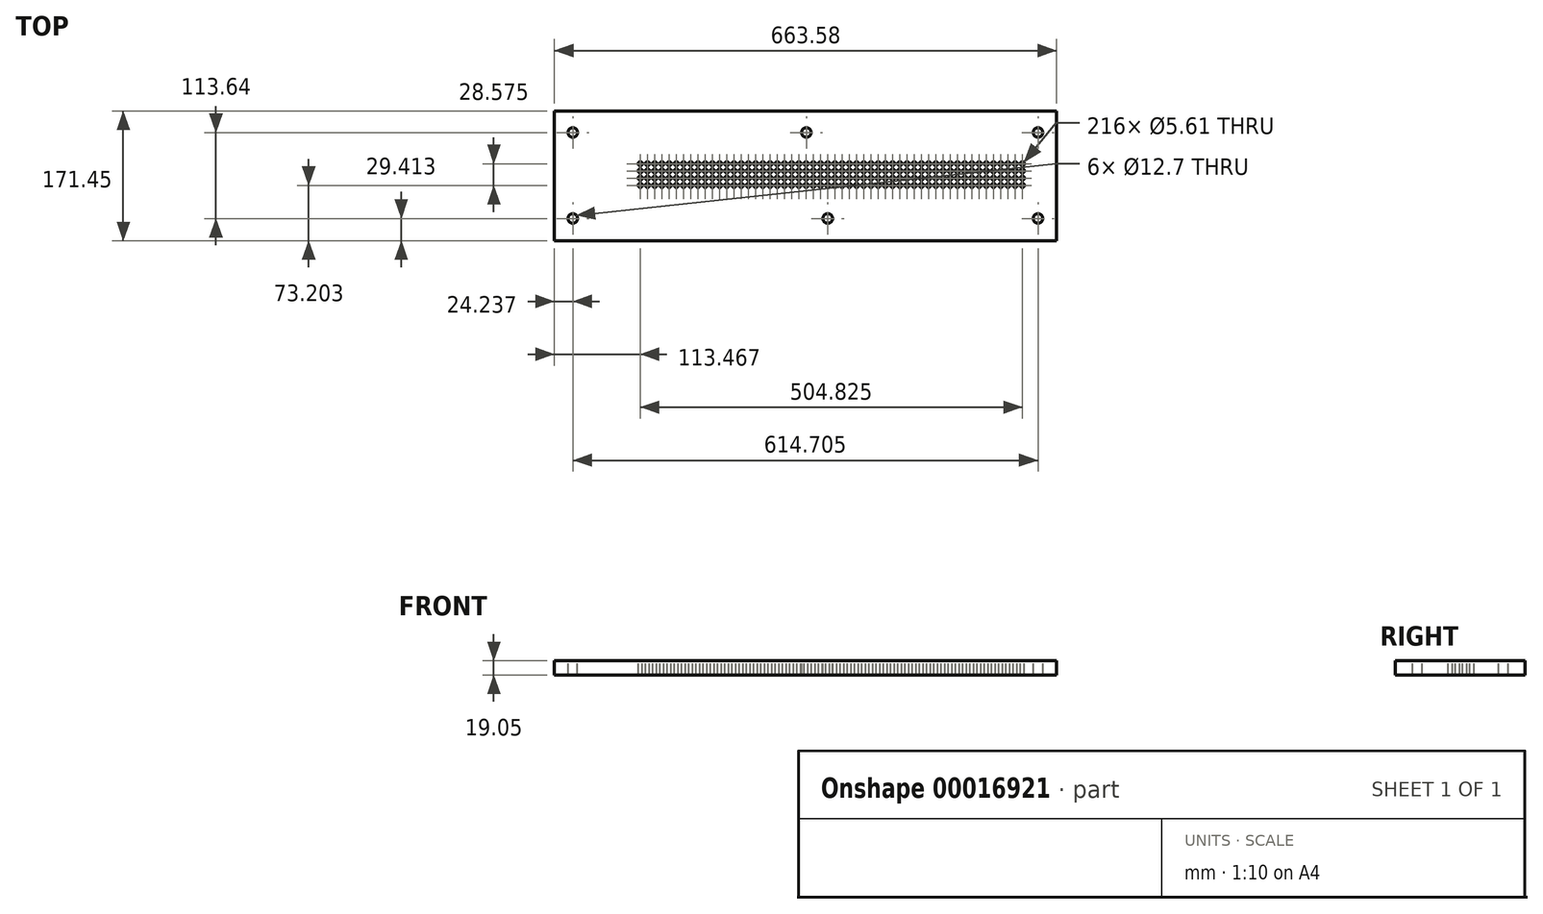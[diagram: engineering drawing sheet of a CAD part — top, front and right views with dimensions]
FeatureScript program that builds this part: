
annotation { "Feature Type Name" : "Feature", "Feature Type Description" : "" }
export const myFeature = defineFeature(function(context is Context, id is Id, definition is map)
    precondition{}
    {
        {
            var Q0;
            Q0=qCreatedBy(makeId("Top.planeOp"),FACE);
            var sketch = newSketch(context, id + "F0", { "sketchPlane" : qUnion([Q0])});
            skLineSegment(sketch, "E0.bottom", {"start": v(0, 0) * mm, "end": v(-663.58, 0) * mm});
            skLineSegment(sketch, "E0.top", {"start": v(0, -171.45) * mm, "end": v(-663.58, -171.45) * mm});
            skLineSegment(sketch, "E0.left", {"start": v(0, 0) * mm, "end": v(0, -171.45) * mm});
            skLineSegment(sketch, "E0.right", {"start": v(-663.58, 0) * mm, "end": v(-663.58, -171.45) * mm});
            skSolve(sketch);
        }
        {
            var Q0;
            Q0 = qSketchRegion(id + "F0", true);
            extrude(context, id + "F1", {"entities" : qUnion([Q0]), "oppositeDirection" : true, "depth" : 19.05 * mm});
        }
        {
            var Q0;
            Q0=makeQuery(id+"F1.opExtrude","CAP_FACE",FACE,{"disambiguationData":[OSD([sQuery(id+"F0.wireOp",EDGE,"E0.bottom"),sQuery(id+"F0.wireOp",EDGE,"E0.top"),sQuery(id+"F0.wireOp",EDGE,"E0.left"),sQuery(id+"F0.wireOp",EDGE,"E0.right")])],"isStart":true});
            var sketch = newSketch(context, id + "F2", { "sketchPlane" : qUnion([Q0])});
            skCircle(sketch, "E1", {"center": v(-24.64, -28.4) * mm, "radius": 6.35 * mm});
            skCircle(sketch, "E2", {"center": v(-330.7, -28.4) * mm, "radius": 6.35 * mm});
            skCircle(sketch, "E3", {"center": v(-639.34, -28.4) * mm, "radius": 6.35 * mm});
            skCircle(sketch, "E4", {"center": v(-639.34, -142.04) * mm, "radius": 6.35 * mm});
            skCircle(sketch, "E5", {"center": v(-302.49, -142.04) * mm, "radius": 6.35 * mm});
            skCircle(sketch, "E6", {"center": v(-24.64, -142.04) * mm, "radius": 6.35 * mm});
            skSolve(sketch);
        }
        {
            var Q0;
            Q0 = qSketchRegion(id + "F2", true);
            extrude(context, id + "F3", {"entities" : qUnion([Q0]), "operationType" : NewBodyOperationType.REMOVE, "endBound" : BoundingType.THROUGH_ALL, "oppositeDirection" : true, "depth" : 25.4 * mm});
        }
        {
            var Q0;
            Q0=makeQuery(id+"F1.opExtrude","CAP_FACE",FACE,{"disambiguationData":[OSD([sQuery(id+"F0.wireOp",EDGE,"E0.bottom"),sQuery(id+"F0.wireOp",EDGE,"E0.top"),sQuery(id+"F0.wireOp",EDGE,"E0.left"),sQuery(id+"F0.wireOp",EDGE,"E0.right")])],"isStart":true});
            var sketch = newSketch(context, id + "F4", { "sketchPlane" : qUnion([Q0])});
            skCircle(sketch, "E7", {"center": v(-45.29, -69.67) * mm, "radius": 2.8 * mm});
            skCircle(sketch, "E8.0.1.0", {"center": v(-45.29, -79.2) * mm, "radius": 2.8 * mm});
            skCircle(sketch, "E8.0.2.0", {"center": v(-45.29, -88.72) * mm, "radius": 2.8 * mm});
            skCircle(sketch, "E8.0.3.0", {"center": v(-45.29, -98.25) * mm, "radius": 2.8 * mm});
            skCircle(sketch, "E8.1.0.0", {"center": v(-54.81, -69.67) * mm, "radius": 2.8 * mm});
            skCircle(sketch, "E8.1.1.0", {"center": v(-54.81, -79.2) * mm, "radius": 2.8 * mm});
            skCircle(sketch, "E8.1.2.0", {"center": v(-54.81, -88.72) * mm, "radius": 2.8 * mm});
            skCircle(sketch, "E8.1.3.0", {"center": v(-54.81, -98.25) * mm, "radius": 2.8 * mm});
            skCircle(sketch, "E8.2.0.0", {"center": v(-64.34, -69.67) * mm, "radius": 2.8 * mm});
            skCircle(sketch, "E8.2.1.0", {"center": v(-64.34, -79.2) * mm, "radius": 2.8 * mm});
            skCircle(sketch, "E8.2.2.0", {"center": v(-64.34, -88.72) * mm, "radius": 2.8 * mm});
            skCircle(sketch, "E8.2.3.0", {"center": v(-64.34, -98.25) * mm, "radius": 2.8 * mm});
            skCircle(sketch, "E8.3.0.0", {"center": v(-73.86, -69.67) * mm, "radius": 2.8 * mm});
            skCircle(sketch, "E8.3.1.0", {"center": v(-73.86, -79.2) * mm, "radius": 2.8 * mm});
            skCircle(sketch, "E8.3.2.0", {"center": v(-73.86, -88.72) * mm, "radius": 2.8 * mm});
            skCircle(sketch, "E8.3.3.0", {"center": v(-73.86, -98.25) * mm, "radius": 2.8 * mm});
            skCircle(sketch, "E8.4.0.0", {"center": v(-83.39, -69.67) * mm, "radius": 2.8 * mm});
            skCircle(sketch, "E8.4.1.0", {"center": v(-83.39, -79.2) * mm, "radius": 2.8 * mm});
            skCircle(sketch, "E8.4.2.0", {"center": v(-83.39, -88.72) * mm, "radius": 2.8 * mm});
            skCircle(sketch, "E8.4.3.0", {"center": v(-83.39, -98.25) * mm, "radius": 2.8 * mm});
            skCircle(sketch, "E8.5.0.0", {"center": v(-92.91, -69.67) * mm, "radius": 2.8 * mm});
            skCircle(sketch, "E8.5.1.0", {"center": v(-92.91, -79.2) * mm, "radius": 2.8 * mm});
            skCircle(sketch, "E8.5.2.0", {"center": v(-92.91, -88.72) * mm, "radius": 2.8 * mm});
            skCircle(sketch, "E8.5.3.0", {"center": v(-92.91, -98.25) * mm, "radius": 2.8 * mm});
            skCircle(sketch, "E8.6.0.0", {"center": v(-102.44, -69.67) * mm, "radius": 2.8 * mm});
            skCircle(sketch, "E8.6.1.0", {"center": v(-102.44, -79.2) * mm, "radius": 2.8 * mm});
            skCircle(sketch, "E8.6.2.0", {"center": v(-102.44, -88.72) * mm, "radius": 2.8 * mm});
            skCircle(sketch, "E8.6.3.0", {"center": v(-102.44, -98.25) * mm, "radius": 2.8 * mm});
            skCircle(sketch, "E8.7.0.0", {"center": v(-111.96, -69.67) * mm, "radius": 2.8 * mm});
            skCircle(sketch, "E8.7.1.0", {"center": v(-111.96, -79.2) * mm, "radius": 2.8 * mm});
            skCircle(sketch, "E8.7.2.0", {"center": v(-111.96, -88.72) * mm, "radius": 2.8 * mm});
            skCircle(sketch, "E8.7.3.0", {"center": v(-111.96, -98.25) * mm, "radius": 2.8 * mm});
            skCircle(sketch, "E8.8.0.0", {"center": v(-121.49, -69.67) * mm, "radius": 2.8 * mm});
            skCircle(sketch, "E8.8.1.0", {"center": v(-121.49, -79.2) * mm, "radius": 2.8 * mm});
            skCircle(sketch, "E8.8.2.0", {"center": v(-121.49, -88.72) * mm, "radius": 2.8 * mm});
            skCircle(sketch, "E8.8.3.0", {"center": v(-121.49, -98.25) * mm, "radius": 2.8 * mm});
            skCircle(sketch, "E8.9.0.0", {"center": v(-131.01, -69.67) * mm, "radius": 2.8 * mm});
            skCircle(sketch, "E8.9.1.0", {"center": v(-131.01, -79.2) * mm, "radius": 2.8 * mm});
            skCircle(sketch, "E8.9.2.0", {"center": v(-131.01, -88.72) * mm, "radius": 2.8 * mm});
            skCircle(sketch, "E8.9.3.0", {"center": v(-131.01, -98.25) * mm, "radius": 2.8 * mm});
            skCircle(sketch, "E8.10.0.0", {"center": v(-140.54, -69.67) * mm, "radius": 2.8 * mm});
            skCircle(sketch, "E8.10.1.0", {"center": v(-140.54, -79.2) * mm, "radius": 2.8 * mm});
            skCircle(sketch, "E8.10.2.0", {"center": v(-140.54, -88.72) * mm, "radius": 2.8 * mm});
            skCircle(sketch, "E8.10.3.0", {"center": v(-140.54, -98.25) * mm, "radius": 2.8 * mm});
            skCircle(sketch, "E8.11.0.0", {"center": v(-150.06, -69.67) * mm, "radius": 2.8 * mm});
            skCircle(sketch, "E8.11.1.0", {"center": v(-150.06, -79.2) * mm, "radius": 2.8 * mm});
            skCircle(sketch, "E8.11.2.0", {"center": v(-150.06, -88.72) * mm, "radius": 2.8 * mm});
            skCircle(sketch, "E8.11.3.0", {"center": v(-150.06, -98.25) * mm, "radius": 2.8 * mm});
            skCircle(sketch, "E8.12.0.0", {"center": v(-159.59, -69.67) * mm, "radius": 2.8 * mm});
            skCircle(sketch, "E8.12.1.0", {"center": v(-159.59, -79.2) * mm, "radius": 2.8 * mm});
            skCircle(sketch, "E8.12.2.0", {"center": v(-159.59, -88.72) * mm, "radius": 2.8 * mm});
            skCircle(sketch, "E8.12.3.0", {"center": v(-159.59, -98.25) * mm, "radius": 2.8 * mm});
            skCircle(sketch, "E8.13.0.0", {"center": v(-169.11, -69.67) * mm, "radius": 2.8 * mm});
            skCircle(sketch, "E8.13.1.0", {"center": v(-169.11, -79.2) * mm, "radius": 2.8 * mm});
            skCircle(sketch, "E8.13.2.0", {"center": v(-169.11, -88.72) * mm, "radius": 2.8 * mm});
            skCircle(sketch, "E8.13.3.0", {"center": v(-169.11, -98.25) * mm, "radius": 2.8 * mm});
            skCircle(sketch, "E8.14.0.0", {"center": v(-178.64, -69.67) * mm, "radius": 2.8 * mm});
            skCircle(sketch, "E8.14.1.0", {"center": v(-178.64, -79.2) * mm, "radius": 2.8 * mm});
            skCircle(sketch, "E8.14.2.0", {"center": v(-178.64, -88.72) * mm, "radius": 2.8 * mm});
            skCircle(sketch, "E8.14.3.0", {"center": v(-178.64, -98.25) * mm, "radius": 2.8 * mm});
            skCircle(sketch, "E8.15.0.0", {"center": v(-188.16, -69.67) * mm, "radius": 2.8 * mm});
            skCircle(sketch, "E8.15.1.0", {"center": v(-188.16, -79.2) * mm, "radius": 2.8 * mm});
            skCircle(sketch, "E8.15.2.0", {"center": v(-188.16, -88.72) * mm, "radius": 2.8 * mm});
            skCircle(sketch, "E8.15.3.0", {"center": v(-188.16, -98.25) * mm, "radius": 2.8 * mm});
            skCircle(sketch, "E8.16.0.0", {"center": v(-197.69, -69.67) * mm, "radius": 2.8 * mm});
            skCircle(sketch, "E8.16.1.0", {"center": v(-197.69, -79.2) * mm, "radius": 2.8 * mm});
            skCircle(sketch, "E8.16.2.0", {"center": v(-197.69, -88.72) * mm, "radius": 2.8 * mm});
            skCircle(sketch, "E8.16.3.0", {"center": v(-197.69, -98.25) * mm, "radius": 2.8 * mm});
            skCircle(sketch, "E8.17.0.0", {"center": v(-207.21, -69.67) * mm, "radius": 2.8 * mm});
            skCircle(sketch, "E8.17.1.0", {"center": v(-207.21, -79.2) * mm, "radius": 2.8 * mm});
            skCircle(sketch, "E8.17.2.0", {"center": v(-207.21, -88.72) * mm, "radius": 2.8 * mm});
            skCircle(sketch, "E8.17.3.0", {"center": v(-207.21, -98.25) * mm, "radius": 2.8 * mm});
            skCircle(sketch, "E8.18.0.0", {"center": v(-216.74, -69.67) * mm, "radius": 2.8 * mm});
            skCircle(sketch, "E8.18.1.0", {"center": v(-216.74, -79.2) * mm, "radius": 2.8 * mm});
            skCircle(sketch, "E8.18.2.0", {"center": v(-216.74, -88.72) * mm, "radius": 2.8 * mm});
            skCircle(sketch, "E8.18.3.0", {"center": v(-216.74, -98.25) * mm, "radius": 2.8 * mm});
            skCircle(sketch, "E8.19.0.0", {"center": v(-226.26, -69.67) * mm, "radius": 2.8 * mm});
            skCircle(sketch, "E8.19.1.0", {"center": v(-226.26, -79.2) * mm, "radius": 2.8 * mm});
            skCircle(sketch, "E8.19.2.0", {"center": v(-226.26, -88.72) * mm, "radius": 2.8 * mm});
            skCircle(sketch, "E8.19.3.0", {"center": v(-226.26, -98.25) * mm, "radius": 2.8 * mm});
            skCircle(sketch, "E8.20.0.0", {"center": v(-235.79, -69.67) * mm, "radius": 2.8 * mm});
            skCircle(sketch, "E8.20.1.0", {"center": v(-235.79, -79.2) * mm, "radius": 2.8 * mm});
            skCircle(sketch, "E8.20.2.0", {"center": v(-235.79, -88.72) * mm, "radius": 2.8 * mm});
            skCircle(sketch, "E8.20.3.0", {"center": v(-235.79, -98.25) * mm, "radius": 2.8 * mm});
            skCircle(sketch, "E8.21.0.0", {"center": v(-245.31, -69.67) * mm, "radius": 2.8 * mm});
            skCircle(sketch, "E8.21.1.0", {"center": v(-245.31, -79.2) * mm, "radius": 2.8 * mm});
            skCircle(sketch, "E8.21.2.0", {"center": v(-245.31, -88.72) * mm, "radius": 2.8 * mm});
            skCircle(sketch, "E8.21.3.0", {"center": v(-245.31, -98.25) * mm, "radius": 2.8 * mm});
            skCircle(sketch, "E8.22.0.0", {"center": v(-254.84, -69.67) * mm, "radius": 2.8 * mm});
            skCircle(sketch, "E8.22.1.0", {"center": v(-254.84, -79.2) * mm, "radius": 2.8 * mm});
            skCircle(sketch, "E8.22.2.0", {"center": v(-254.84, -88.72) * mm, "radius": 2.8 * mm});
            skCircle(sketch, "E8.22.3.0", {"center": v(-254.84, -98.25) * mm, "radius": 2.8 * mm});
            skCircle(sketch, "E8.23.0.0", {"center": v(-264.36, -69.67) * mm, "radius": 2.8 * mm});
            skCircle(sketch, "E8.23.1.0", {"center": v(-264.36, -79.2) * mm, "radius": 2.8 * mm});
            skCircle(sketch, "E8.23.2.0", {"center": v(-264.36, -88.72) * mm, "radius": 2.8 * mm});
            skCircle(sketch, "E8.23.3.0", {"center": v(-264.36, -98.25) * mm, "radius": 2.8 * mm});
            skCircle(sketch, "E8.24.0.0", {"center": v(-273.89, -69.67) * mm, "radius": 2.8 * mm});
            skCircle(sketch, "E8.24.1.0", {"center": v(-273.89, -79.2) * mm, "radius": 2.8 * mm});
            skCircle(sketch, "E8.24.2.0", {"center": v(-273.89, -88.72) * mm, "radius": 2.8 * mm});
            skCircle(sketch, "E8.24.3.0", {"center": v(-273.89, -98.25) * mm, "radius": 2.8 * mm});
            skCircle(sketch, "E8.25.0.0", {"center": v(-283.41, -69.67) * mm, "radius": 2.8 * mm});
            skCircle(sketch, "E8.25.1.0", {"center": v(-283.41, -79.2) * mm, "radius": 2.8 * mm});
            skCircle(sketch, "E8.25.2.0", {"center": v(-283.41, -88.72) * mm, "radius": 2.8 * mm});
            skCircle(sketch, "E8.25.3.0", {"center": v(-283.41, -98.25) * mm, "radius": 2.8 * mm});
            skCircle(sketch, "E8.26.0.0", {"center": v(-292.94, -69.67) * mm, "radius": 2.8 * mm});
            skCircle(sketch, "E8.26.1.0", {"center": v(-292.94, -79.2) * mm, "radius": 2.8 * mm});
            skCircle(sketch, "E8.26.2.0", {"center": v(-292.94, -88.72) * mm, "radius": 2.8 * mm});
            skCircle(sketch, "E8.26.3.0", {"center": v(-292.94, -98.25) * mm, "radius": 2.8 * mm});
            skCircle(sketch, "E8.27.0.0", {"center": v(-302.46, -69.67) * mm, "radius": 2.8 * mm});
            skCircle(sketch, "E8.27.1.0", {"center": v(-302.46, -79.2) * mm, "radius": 2.8 * mm});
            skCircle(sketch, "E8.27.2.0", {"center": v(-302.46, -88.72) * mm, "radius": 2.8 * mm});
            skCircle(sketch, "E8.27.3.0", {"center": v(-302.46, -98.25) * mm, "radius": 2.8 * mm});
            skCircle(sketch, "E8.28.0.0", {"center": v(-311.99, -69.67) * mm, "radius": 2.8 * mm});
            skCircle(sketch, "E8.28.1.0", {"center": v(-311.99, -79.2) * mm, "radius": 2.8 * mm});
            skCircle(sketch, "E8.28.2.0", {"center": v(-311.99, -88.72) * mm, "radius": 2.8 * mm});
            skCircle(sketch, "E8.28.3.0", {"center": v(-311.99, -98.25) * mm, "radius": 2.8 * mm});
            skCircle(sketch, "E8.29.0.0", {"center": v(-321.51, -69.67) * mm, "radius": 2.8 * mm});
            skCircle(sketch, "E8.29.1.0", {"center": v(-321.51, -79.2) * mm, "radius": 2.8 * mm});
            skCircle(sketch, "E8.29.2.0", {"center": v(-321.51, -88.72) * mm, "radius": 2.8 * mm});
            skCircle(sketch, "E8.29.3.0", {"center": v(-321.51, -98.25) * mm, "radius": 2.8 * mm});
            skCircle(sketch, "E8.30.0.0", {"center": v(-331.04, -69.67) * mm, "radius": 2.8 * mm});
            skCircle(sketch, "E8.30.1.0", {"center": v(-331.04, -79.2) * mm, "radius": 2.8 * mm});
            skCircle(sketch, "E8.30.2.0", {"center": v(-331.04, -88.72) * mm, "radius": 2.8 * mm});
            skCircle(sketch, "E8.30.3.0", {"center": v(-331.04, -98.25) * mm, "radius": 2.8 * mm});
            skCircle(sketch, "E8.31.0.0", {"center": v(-340.56, -69.67) * mm, "radius": 2.8 * mm});
            skCircle(sketch, "E8.31.1.0", {"center": v(-340.56, -79.2) * mm, "radius": 2.8 * mm});
            skCircle(sketch, "E8.31.2.0", {"center": v(-340.56, -88.72) * mm, "radius": 2.8 * mm});
            skCircle(sketch, "E8.31.3.0", {"center": v(-340.56, -98.25) * mm, "radius": 2.8 * mm});
            skCircle(sketch, "E8.32.0.0", {"center": v(-350.09, -69.67) * mm, "radius": 2.8 * mm});
            skCircle(sketch, "E8.32.1.0", {"center": v(-350.09, -79.2) * mm, "radius": 2.8 * mm});
            skCircle(sketch, "E8.32.2.0", {"center": v(-350.09, -88.72) * mm, "radius": 2.8 * mm});
            skCircle(sketch, "E8.32.3.0", {"center": v(-350.09, -98.25) * mm, "radius": 2.8 * mm});
            skCircle(sketch, "E8.33.0.0", {"center": v(-359.61, -69.67) * mm, "radius": 2.8 * mm});
            skCircle(sketch, "E8.33.1.0", {"center": v(-359.61, -79.2) * mm, "radius": 2.8 * mm});
            skCircle(sketch, "E8.33.2.0", {"center": v(-359.61, -88.72) * mm, "radius": 2.8 * mm});
            skCircle(sketch, "E8.33.3.0", {"center": v(-359.61, -98.25) * mm, "radius": 2.8 * mm});
            skCircle(sketch, "E8.34.0.0", {"center": v(-369.14, -69.67) * mm, "radius": 2.8 * mm});
            skCircle(sketch, "E8.34.1.0", {"center": v(-369.14, -79.2) * mm, "radius": 2.8 * mm});
            skCircle(sketch, "E8.34.2.0", {"center": v(-369.14, -88.72) * mm, "radius": 2.8 * mm});
            skCircle(sketch, "E8.34.3.0", {"center": v(-369.14, -98.25) * mm, "radius": 2.8 * mm});
            skCircle(sketch, "E8.35.0.0", {"center": v(-378.66, -69.67) * mm, "radius": 2.8 * mm});
            skCircle(sketch, "E8.35.1.0", {"center": v(-378.66, -79.2) * mm, "radius": 2.8 * mm});
            skCircle(sketch, "E8.35.2.0", {"center": v(-378.66, -88.72) * mm, "radius": 2.8 * mm});
            skCircle(sketch, "E8.35.3.0", {"center": v(-378.66, -98.25) * mm, "radius": 2.8 * mm});
            skCircle(sketch, "E8.36.0.0", {"center": v(-388.19, -69.67) * mm, "radius": 2.8 * mm});
            skCircle(sketch, "E8.36.1.0", {"center": v(-388.19, -79.2) * mm, "radius": 2.8 * mm});
            skCircle(sketch, "E8.36.2.0", {"center": v(-388.19, -88.72) * mm, "radius": 2.8 * mm});
            skCircle(sketch, "E8.36.3.0", {"center": v(-388.19, -98.25) * mm, "radius": 2.8 * mm});
            skCircle(sketch, "E8.37.0.0", {"center": v(-397.71, -69.67) * mm, "radius": 2.8 * mm});
            skCircle(sketch, "E8.37.1.0", {"center": v(-397.71, -79.2) * mm, "radius": 2.8 * mm});
            skCircle(sketch, "E8.37.2.0", {"center": v(-397.71, -88.72) * mm, "radius": 2.8 * mm});
            skCircle(sketch, "E8.37.3.0", {"center": v(-397.71, -98.25) * mm, "radius": 2.8 * mm});
            skCircle(sketch, "E8.38.0.0", {"center": v(-407.24, -69.67) * mm, "radius": 2.8 * mm});
            skCircle(sketch, "E8.38.1.0", {"center": v(-407.24, -79.2) * mm, "radius": 2.8 * mm});
            skCircle(sketch, "E8.38.2.0", {"center": v(-407.24, -88.72) * mm, "radius": 2.8 * mm});
            skCircle(sketch, "E8.38.3.0", {"center": v(-407.24, -98.25) * mm, "radius": 2.8 * mm});
            skCircle(sketch, "E8.39.0.0", {"center": v(-416.76, -69.67) * mm, "radius": 2.8 * mm});
            skCircle(sketch, "E8.39.1.0", {"center": v(-416.76, -79.2) * mm, "radius": 2.8 * mm});
            skCircle(sketch, "E8.39.2.0", {"center": v(-416.76, -88.72) * mm, "radius": 2.8 * mm});
            skCircle(sketch, "E8.39.3.0", {"center": v(-416.76, -98.25) * mm, "radius": 2.8 * mm});
            skCircle(sketch, "E8.40.0.0", {"center": v(-426.29, -69.67) * mm, "radius": 2.8 * mm});
            skCircle(sketch, "E8.40.1.0", {"center": v(-426.29, -79.2) * mm, "radius": 2.8 * mm});
            skCircle(sketch, "E8.40.2.0", {"center": v(-426.29, -88.72) * mm, "radius": 2.8 * mm});
            skCircle(sketch, "E8.40.3.0", {"center": v(-426.29, -98.25) * mm, "radius": 2.8 * mm});
            skCircle(sketch, "E8.41.0.0", {"center": v(-435.81, -69.67) * mm, "radius": 2.8 * mm});
            skCircle(sketch, "E8.41.1.0", {"center": v(-435.81, -79.2) * mm, "radius": 2.8 * mm});
            skCircle(sketch, "E8.41.2.0", {"center": v(-435.81, -88.72) * mm, "radius": 2.8 * mm});
            skCircle(sketch, "E8.41.3.0", {"center": v(-435.81, -98.25) * mm, "radius": 2.8 * mm});
            skCircle(sketch, "E8.42.0.0", {"center": v(-445.34, -69.67) * mm, "radius": 2.8 * mm});
            skCircle(sketch, "E8.42.1.0", {"center": v(-445.34, -79.2) * mm, "radius": 2.8 * mm});
            skCircle(sketch, "E8.42.2.0", {"center": v(-445.34, -88.72) * mm, "radius": 2.8 * mm});
            skCircle(sketch, "E8.42.3.0", {"center": v(-445.34, -98.25) * mm, "radius": 2.8 * mm});
            skCircle(sketch, "E8.43.0.0", {"center": v(-454.86, -69.67) * mm, "radius": 2.8 * mm});
            skCircle(sketch, "E8.43.1.0", {"center": v(-454.86, -79.2) * mm, "radius": 2.8 * mm});
            skCircle(sketch, "E8.43.2.0", {"center": v(-454.86, -88.72) * mm, "radius": 2.8 * mm});
            skCircle(sketch, "E8.43.3.0", {"center": v(-454.86, -98.25) * mm, "radius": 2.8 * mm});
            skCircle(sketch, "E8.44.0.0", {"center": v(-464.39, -69.67) * mm, "radius": 2.8 * mm});
            skCircle(sketch, "E8.44.1.0", {"center": v(-464.39, -79.2) * mm, "radius": 2.8 * mm});
            skCircle(sketch, "E8.44.2.0", {"center": v(-464.39, -88.72) * mm, "radius": 2.8 * mm});
            skCircle(sketch, "E8.44.3.0", {"center": v(-464.39, -98.25) * mm, "radius": 2.8 * mm});
            skCircle(sketch, "E8.45.0.0", {"center": v(-473.91, -69.67) * mm, "radius": 2.8 * mm});
            skCircle(sketch, "E8.45.1.0", {"center": v(-473.91, -79.2) * mm, "radius": 2.8 * mm});
            skCircle(sketch, "E8.45.2.0", {"center": v(-473.91, -88.72) * mm, "radius": 2.8 * mm});
            skCircle(sketch, "E8.45.3.0", {"center": v(-473.91, -98.25) * mm, "radius": 2.8 * mm});
            skCircle(sketch, "E8.46.0.0", {"center": v(-483.44, -69.67) * mm, "radius": 2.8 * mm});
            skCircle(sketch, "E8.46.1.0", {"center": v(-483.44, -79.2) * mm, "radius": 2.8 * mm});
            skCircle(sketch, "E8.46.2.0", {"center": v(-483.44, -88.72) * mm, "radius": 2.8 * mm});
            skCircle(sketch, "E8.46.3.0", {"center": v(-483.44, -98.25) * mm, "radius": 2.8 * mm});
            skCircle(sketch, "E8.47.0.0", {"center": v(-492.96, -69.67) * mm, "radius": 2.8 * mm});
            skCircle(sketch, "E8.47.1.0", {"center": v(-492.96, -79.2) * mm, "radius": 2.8 * mm});
            skCircle(sketch, "E8.47.2.0", {"center": v(-492.96, -88.72) * mm, "radius": 2.8 * mm});
            skCircle(sketch, "E8.47.3.0", {"center": v(-492.96, -98.25) * mm, "radius": 2.8 * mm});
            skCircle(sketch, "E8.48.0.0", {"center": v(-502.49, -69.67) * mm, "radius": 2.8 * mm});
            skCircle(sketch, "E8.48.1.0", {"center": v(-502.49, -79.2) * mm, "radius": 2.8 * mm});
            skCircle(sketch, "E8.48.2.0", {"center": v(-502.49, -88.72) * mm, "radius": 2.8 * mm});
            skCircle(sketch, "E8.48.3.0", {"center": v(-502.49, -98.25) * mm, "radius": 2.8 * mm});
            skCircle(sketch, "E8.49.0.0", {"center": v(-512.01, -69.67) * mm, "radius": 2.8 * mm});
            skCircle(sketch, "E8.49.1.0", {"center": v(-512.01, -79.2) * mm, "radius": 2.8 * mm});
            skCircle(sketch, "E8.49.2.0", {"center": v(-512.01, -88.72) * mm, "radius": 2.8 * mm});
            skCircle(sketch, "E8.49.3.0", {"center": v(-512.01, -98.25) * mm, "radius": 2.8 * mm});
            skCircle(sketch, "E8.50.0.0", {"center": v(-521.54, -69.67) * mm, "radius": 2.8 * mm});
            skCircle(sketch, "E8.50.1.0", {"center": v(-521.54, -79.2) * mm, "radius": 2.8 * mm});
            skCircle(sketch, "E8.50.2.0", {"center": v(-521.54, -88.72) * mm, "radius": 2.8 * mm});
            skCircle(sketch, "E8.50.3.0", {"center": v(-521.54, -98.25) * mm, "radius": 2.8 * mm});
            skCircle(sketch, "E8.51.0.0", {"center": v(-531.06, -69.67) * mm, "radius": 2.8 * mm});
            skCircle(sketch, "E8.51.1.0", {"center": v(-531.06, -79.2) * mm, "radius": 2.8 * mm});
            skCircle(sketch, "E8.51.2.0", {"center": v(-531.06, -88.72) * mm, "radius": 2.8 * mm});
            skCircle(sketch, "E8.51.3.0", {"center": v(-531.06, -98.25) * mm, "radius": 2.8 * mm});
            skCircle(sketch, "E8.52.0.0", {"center": v(-540.59, -69.67) * mm, "radius": 2.8 * mm});
            skCircle(sketch, "E8.52.1.0", {"center": v(-540.59, -79.2) * mm, "radius": 2.8 * mm});
            skCircle(sketch, "E8.52.2.0", {"center": v(-540.59, -88.72) * mm, "radius": 2.8 * mm});
            skCircle(sketch, "E8.52.3.0", {"center": v(-540.59, -98.25) * mm, "radius": 2.8 * mm});
            skCircle(sketch, "E8.53.0.0", {"center": v(-550.11, -69.67) * mm, "radius": 2.8 * mm});
            skCircle(sketch, "E8.53.1.0", {"center": v(-550.11, -79.2) * mm, "radius": 2.8 * mm});
            skCircle(sketch, "E8.53.2.0", {"center": v(-550.11, -88.72) * mm, "radius": 2.8 * mm});
            skCircle(sketch, "E8.53.3.0", {"center": v(-550.11, -98.25) * mm, "radius": 2.8 * mm});
            skLineSegment(sketch, "E8.direction1", {"start": v(-45.29, -69.67) * mm, "end": v(-54.81, -69.67) * mm, "construction": true});
            skLineSegment(sketch, "E8.direction2", {"start": v(-45.29, -69.67) * mm, "end": v(-45.29, -79.2) * mm, "construction": true});
            skSolve(sketch);
        }
        {
            var Q0;
            Q0 = qSketchRegion(id + "F4", true);
            extrude(context, id + "F5", {"entities" : qUnion([Q0]), "operationType" : NewBodyOperationType.REMOVE, "endBound" : BoundingType.THROUGH_ALL, "oppositeDirection" : true, "depth" : 25.4 * mm});
        }
    });
